# Revit family: XL Commercial Cylinder
name_source: partatom
category: Generic Models
revit_build: Autodesk Revit 2018 (Build: 20170223_1515(x64)
units: mm (PartAtom-declared; Revit-internal decimal feet)

## family parameters
Can host rebar = No
Cut with Voids When Loaded = No
Host = Face
Part Type = Normal
Room Calculation Point = No
Round Connector Dimension = Use Diameter
Shared = No

## types (3) — shared parameters
Cold Water Connection Diameter = 2"
Cold Water Pressure Relief Valve = 700 kPa (approx.)
Construction = 2205 Duplex Stainless Steel
Default Elevation = 2318 mm  [stored 7.60499 ft]
Delivery Temperatures = Must comply with G12 6.14 Safe water temperatures
Hot Outlet Connection Diameter = 2"
Insulation = Polyurethane Foam
Load Demand Coefficient = 1.8
Pressure Limiting Valve - 1000kPa (approx.) = If the water supply pressure exceeds the rated pressure a pressure limiting valve is to be fitted to the installation
Pressure Rating = 1200 kPa
Secondary Return Connection Diameter = 2"
TPR Connection Diameter = 1 1/4"
Valve Supplied (TPR - 1000 kPa , 25mm, 132 kW) = One TPR valve is supplied with each cylinder. If additional valves are required these can be ordered separately.
Warranty = 10 years—cylinder is warranted to a maximum temperature of 95 °C

## per-type parameters (varying)
| type | Cold Inlet/ Sensor Pocket Height | Connection Radii | Constraint | Cylinder Height | Heat Loss 24 hrs @ 65°C | Hot Outlet Height | Lateral Force on Tank | Sec. Return Height | TPR Height | Weight Calculation | Weights empty/full |
| 1000L | 557 mm | 505 mm | 1 | 2318 mm  [stored 7.60499 ft] | 3 kWh | 1742 mm | 20.69 kN | 769 mm | 1892 mm | 11.50 kN | 178 kg / 1178 kg |
| 800L | 557 mm | 505 mm | 2 | 1923 mm  [stored 6.30906 ft] | 3 kWh | 1347 mm  [stored 4.41929 ft] | 16.81 kN | 767 mm  [stored 2.5164 ft] | 1487 mm  [stored 4.87861 ft] | 9.30 kN | 153 kg / 953 kg |
| 500L | 496 mm  [stored 1.6273 ft] | 430 mm | 3 | 1820 mm | 2 kWh | 1301 mm  [stored 4.26837 ft] | 10.56 kN | 696 mm  [stored 2.28346 ft] | 1421 mm  [stored 4.66207 ft] | 5.90 kN | 99 kg / 599 kg |

note: [stored X ft] marks values corroborated as IEEE doubles in the binary element streams (Revit-internal decimal feet)

## geometry (parser evidence)
native form markers: Sweep x2
no freeform markers — native parametric forms only
